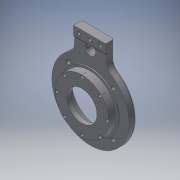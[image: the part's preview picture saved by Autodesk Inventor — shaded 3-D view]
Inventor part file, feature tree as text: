
AUTODESK INVENTOR PART (.ipt)
format: ipt  version: 2019.4 (Build 234330000, 330)  size: 329,728 bytes
history: native  units: mm
features: sketch x14, extrude x11, fillet x5, pattern_circular x3, hole x3, projected_geometry x3, pattern_linear x1, chamfer x1
ambient origin geometry x8: Origin, YZ Plane, XZ Plane, XY Plane, X Axis, Y Axis, Z Axis, Center Point
bodies: Solid1 (feature_tree)
feature tree (41):
  extrude  "Extrusion1"  Depth=72.0mm
  extrude  "Extrusion2"  Depth=49.95mm
  extrude  "Extrusion5"  Depth=28.0mm
  extrude  "Extrusion3"  Depth=3.05mm
  extrude  "Extrusion4"  Depth=80.0mm TaperAngle=360.0deg
  pattern_circular  "Circular Pattern1"  Count=3  [1 undecoded]
  extrude  "Extrusion6"  Depth=3.0mm TaperAngle=0.0deg
  extrude  "Extrusion7"  Depth=10.0mm
  extrude  "Extrusion8"  Depth=3.0mm TaperAngle=0.0deg
  fillet  "Fillet1"  Radius=3.0mm
  extrude  "Extrusion9"  Depth=6.0mm
  fillet  "Fillet2"  Radius=4.0mm
  hole  "Hole1"  [1 undecoded]
  pattern_linear  "Rectangular Pattern1"  Count1=2 Spacing1=10.0mm
  fillet  "Fillet3"  Radius=1.0mm
  extrude  "Extrusion10"  Depth=10.0mm
  hole  "Hole2"  [1 undecoded]
  pattern_circular  "Circular Pattern2"  Count=8 Angle=360.0deg
  fillet  "Fillet5"  Radius=14.5mm
  extrude  "Extrusion11"  Depth=5.0mm TaperAngle=360.0deg
  fillet  "Fillet6"  Radius=2.0mm
  hole  "Hole3"  [1 undecoded]
  pattern_circular  "Circular Pattern3"  [2 undecoded]
  chamfer  "Chamfer1"  Distance=29.5mm
  sketch  "Sketch1"  dims[d0=50.0mm d1=72.0mm]
  sketch  "Sketch2"  dims[d2=18.0mm d3=0.0mm d4=49.95mm]
  projected_geometry  "Projected Loop1"
  sketch  "Sketch3"  dims[d5=8.0mm d6=0.0mm d7=28.0mm]
  sketch  "Sketch4"  dims[d8=7.0mm d9=0.0mm d10=3.05mm]
  sketch  "Sketch5"  dims[d11=3.5mm d12=0.0mm d13=80.0mm d14=360.0deg]
  sketch  "Sketch6"  dims[d16=54.0mm]
  sketch  "Sketch8"  dims[d17=1.0mm d18=0.0mm]
  sketch  "Sketch9"  dims[d19=45.5mm]
  projected_geometry  "Projected Loop2"
  sketch  "Sketch10"  dims[d20=14.0mm d21=0.0mm d24=30.0mm]
  sketch  "Sketch11"  dims[d25=5.0mm d26=0.0mm d27=3.0mm d28=0.0mm]
  sketch  "Sketch12"  dims[d29=10.0mm d30=8.0mm]
  sketch  "Sketch13"  dims[d31=13.0mm d32=3.0mm d33=0.0mm d34=3.0mm]
  sketch  "Sketch14"  dims[d35=54.0mm d36=6.0mm d37=4.0mm]
  projected_geometry  "Projected Loop3"
  sketch  "Sketch15"  dims[d38=3.1mm d39=6.0mm d40=6.5mm d41=2.0mm d42=90.0deg d43=10.0mm d44=0.0mm d45=20.0mm d47=10.0mm d48=20.0mm d50=10.0mm d51=1.0mm d52=10.0mm d53=29.5mm d54=80.0mm d56=360.0deg d58=14.5mm d59=0.0mm d61=3.88mm d62=6.0mm d63=4.34mm d64=2.0mm d65=1.22173mm d66=7.0mm d67=0.0mm d68=40.0mm d69=360.0deg d71=2.0mm d72=1.0mm d73=0.0mm d74=2.0mm d75=29.5mm d76=45.0deg d77=3.0mm d78=3.88mm d79=6.0mm d80=4.34mm d81=2.0mm d82=1.22173mm d83=7.0mm d84=0.0mm d85=40.0mm d86=360.0deg d88=5.0mm d89=2.0mm d90=45.0deg]
note: 6 required parameter values undecoded (feature->parameter linkage not recoverable at this tier; creation-order binding heuristic only, values carry confidence <= 0.55)
